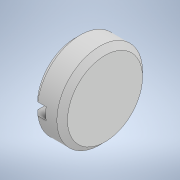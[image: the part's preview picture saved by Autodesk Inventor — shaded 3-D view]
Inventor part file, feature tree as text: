
AUTODESK INVENTOR PART (.ipt)
format: ipt  version: 2022 (Build 260153000, 153)  size: 124,928 bytes
history: native  units: mm
features: other x2, sketch x2, revolve x1, extrude x1
ambient origin geometry x8: Origin, YZ Plane, XZ Plane, XY Plane, X Axis, Y Axis, Z Axis, Center Point
bodies: Body1 (feature_tree)
feature tree (6):
  other  "Твердое тело1"
  revolve  "Вращение1"
  other  "РабПлоскость1"
  extrude  "Выдавливание1"  Depth=20.0mm
  sketch  "Эскиз1"
  sketch  "Эскиз2"
